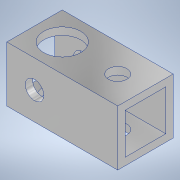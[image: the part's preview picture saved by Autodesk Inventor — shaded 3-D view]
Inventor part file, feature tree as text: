
AUTODESK INVENTOR PART (.ipt)
format: ipt  version: 2020.3 (Build 243373000, 373)  size: 136,704 bytes
history: native  units: mm
features: sketch x4, hole x3, other x1, extrude x1
ambient origin geometry x8: Origin, YZ Plane, XZ Plane, XY Plane, X Axis, Y Axis, Z Axis, Center Point
bodies: Body1 (feature_tree)
feature tree (9):
  other  "ソリッド1"
  extrude  "押し出し1"  Depth=9.0mm
  hole  "穴1"  [1 undecoded]
  hole  "穴2"  [1 undecoded]
  hole  "穴3"  [1 undecoded]
  sketch  "スケッチ1"
  sketch  "スケッチ2"
  sketch  "スケッチ3"
  sketch  "スケッチ4"
note: 3 required parameter values undecoded (feature->parameter linkage not recoverable at this tier; creation-order binding heuristic only, values carry confidence <= 0.55)
